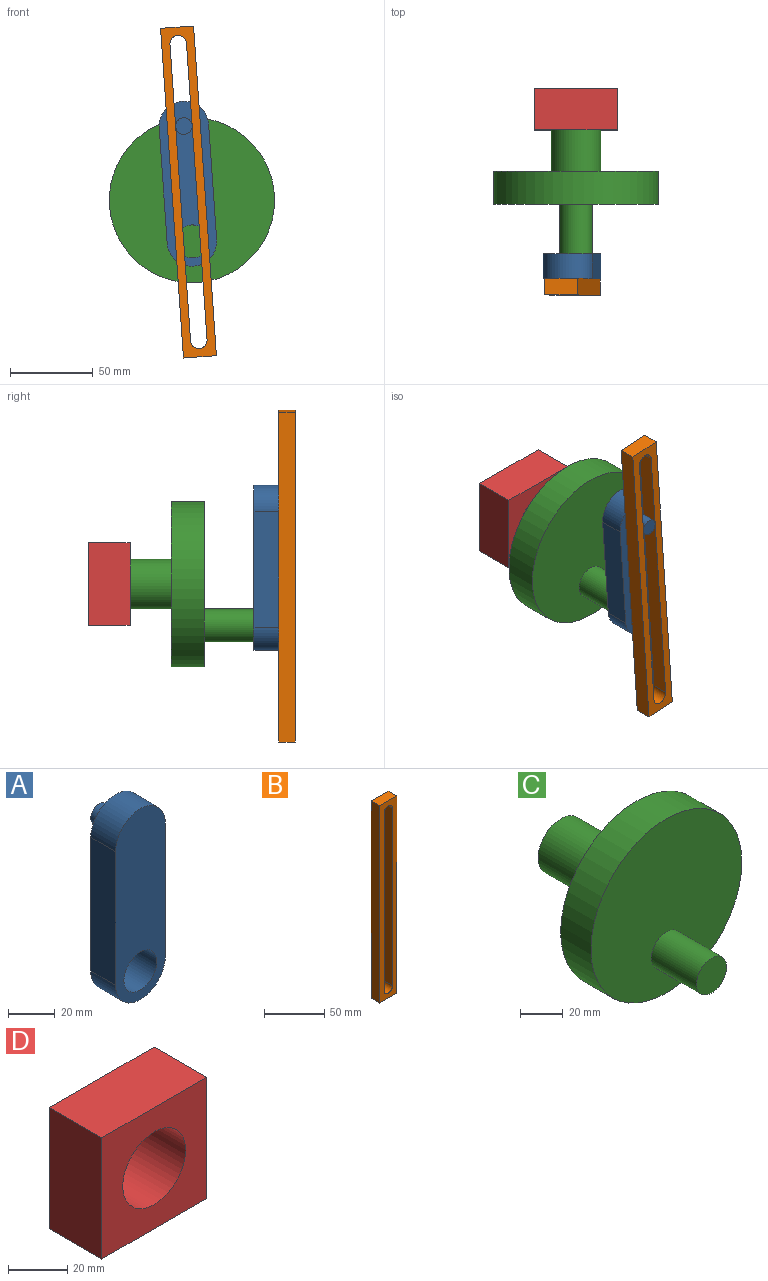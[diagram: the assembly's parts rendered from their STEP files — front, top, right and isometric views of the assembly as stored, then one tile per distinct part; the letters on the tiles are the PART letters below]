
ASSEMBLY  parts=4 mates=3
PART A: 9 faces, bbox 30x25x100 mm
  f0: cylinder r=15mm len=30mm, axis (0,1,0), area 706.9mm2, adj f1,f4,f5,f6
  f1: plane 70x15mm, normal (-1,0,0), area 1050mm2, adj f0,f2,f5,f6
  f2: cylinder r=15mm len=30mm, axis (0,1,0), area 706.9mm2, adj f1,f4,f5,f6
  f3: cylinder r=10mm len=20mm, axis (0,1,0), area 942.5mm2, adj f5,f6
  f4: plane 70x15mm, normal (1,0,0), area 1050mm2, adj f0,f2,f5,f6
  f5: plane 100x30mm, normal (0,-1,0), area 2492.7mm2, adj f0,f1,f2,f3,f4
  f6: plane 100x30mm, normal (0,1,0), area 2414.2mm2, adj f0,f1,f2,f3,f4,f7
  f7: cylinder r=5mm len=10mm, axis (0,-1,0), area 314.2mm2, adj f6,f8
  f8: plane 10x10mm, normal (0,1,0), area 78.5mm2, adj f7
PART B: 10 faces, bbox 20x10x200 mm
  f0: plane 200x10mm, normal (1,0,0), area 2000mm2, adj f1,f7,f8,f9
  f1: plane 20x10mm, normal (0,0,1), area 200mm2, adj f0,f2,f8,f9
  f2: plane 200x10mm, normal (-1,0,0), area 2000mm2, adj f1,f7,f8,f9
  f3: cylinder r=5mm len=10mm, axis (0,1,0), area 157.1mm2, adj f4,f6,f8,f9
  f4: plane 180x10mm, normal (-1,0,0), area 1800mm2, adj f3,f5,f8,f9
  f5: cylinder r=5mm len=10mm, axis (0,1,0), area 157.1mm2, adj f4,f6,f8,f9
  f6: plane 180x10mm, normal (1,0,0), area 1800mm2, adj f3,f5,f8,f9
  f7: plane 20x10mm, normal (0,0,-1), area 200mm2, adj f0,f2,f8,f9
  f8: plane 200x20mm, normal (0,-1,0), area 2121.5mm2, adj f0,f1,f2,f3,f4,f5,f6,f7
  f9: plane 200x20mm, normal (0,1,0), area 2121.5mm2, adj f0,f1,f2,f3,f4,f5,f6,f7
PART C: 7 faces, bbox 100x100x100 mm
  f0: cylinder r=50mm len=100mm, axis (0,1,0), area 6283.2mm2, adj f1,f2
  f1: plane 100x100mm, normal (0,-1,0), area 7539.8mm2, adj f0,f3
  f2: plane 100x100mm, normal (0,1,0), area 7147.1mm2, adj f0,f5
  f3: cylinder r=10mm len=30mm, axis (0,1,0), area 1885mm2, adj f1,f4
  f4: plane 20x20mm, normal (0,-1,0), area 314.2mm2, adj f3
  f5: cylinder r=15mm len=50mm, axis (0,-1,0), area 4712.4mm2, adj f2,f6
  f6: plane 30x30mm, normal (0,1,0), area 706.9mm2, adj f5
PART D: 7 faces, bbox 50x25x50 mm
  f0: plane 50x25mm, normal (1,0,0), area 1250mm2, adj f1,f4,f5,f6
  f1: plane 50x25mm, normal (0,0,1), area 1250mm2, adj f0,f2,f5,f6
  f2: plane 50x25mm, normal (-1,0,0), area 1250mm2, adj f1,f4,f5,f6
  f3: cylinder r=15mm len=30mm, axis (0,1,0), area 2356.2mm2, adj f5,f6
  f4: plane 50x25mm, normal (0,0,-1), area 1250mm2, adj f0,f2,f5,f6
  f5: plane 50x50mm, normal (0,-1,0), area 1793.1mm2, adj f0,f1,f2,f3,f4
  f6: plane 50x50mm, normal (0,1,0), area 1793.1mm2, adj f0,f1,f2,f3,f4
PLACE A rot(axis=(0.03,0,-1),180deg) t=(-4.91,-103.06,11.23)mm
PLACE B rot(axis=(1,0,0.03),180deg) t=(-4.57,-113.06,6.24)mm fixed
PLACE C t=(-2.49,-38.06,1.31)mm
PLACE D t=(-2.49,11.94,1.31)mm fixed
MATE revolute A.f2 <-> C.f3  axis (0,1,0) through (-2.49,-88.06,-23.69)mm
MATE revolute C.f0 <-> D.f3  axis (0,-1,0) through (-2.49,11.94,1.31)mm
MATE pin_slot A.f0 <-> B.f5  axis (0,-1,0) through (-7.33,-113.06,46.14)mm
